# Revit family: Schallentkopplungs-Set K
name_source: partatom
category: Allgemeines Modell
revit_build: Autodesk Revit 2017 (Build: 20190507_1515(x64)
units: mm (PartAtom-declared; Revit-internal decimal feet)

## family parameters
Arbeitsebenenbasiert = Ja
Beim Laden mit Abzugskörper schneiden = Nein
Bemaßung runder Anschluss = Durchmesser verwenden
Gemeinsam genutzt = Ja
Immer vertikal = Nein
Kann Basisbauteil für Bewehrung sein = Nein
Raumberechnungspunkt = Nein
Teiletyp = Normal

## types (1)
- Schallentkopplungs-Set K
    Abmessung = 137x70x6 mm
    Artikelnummer = 077034001
    Breite = 70 mm  [stored 0.229659 ft]
    EAN = 4250928447913
    Fabrikat = MEFA
    Firma = MEFA Befestigungs- und Montagesysteme GmbH
    Gewicht = 0.09 kg
    Gewicht pro Bauteil = 0.09 kg
    Innendurchmesser Hülse = 10,5 mm
    Kurztext1 = Schallentkopplungs-Set Festpunkt
    Kurztext2 = Dämmplatte 137x70x6 mm Hülse 10,5 mm
    Länge = 137 mm  [stored 0.449475 ft]
    Material = Gummi
    Materialname = EPDM
    Mengeneinheit = St
    Stärke = 6 mm  [stored 0.019685 ft]
    Vorgabe-Ansicht = 1219 mm
    max. Temperaturbeständigkeit = 100 °C
    vpe = 1 SET

note: [stored X ft] marks values corroborated as IEEE doubles in the binary element streams (Revit-internal decimal feet)
